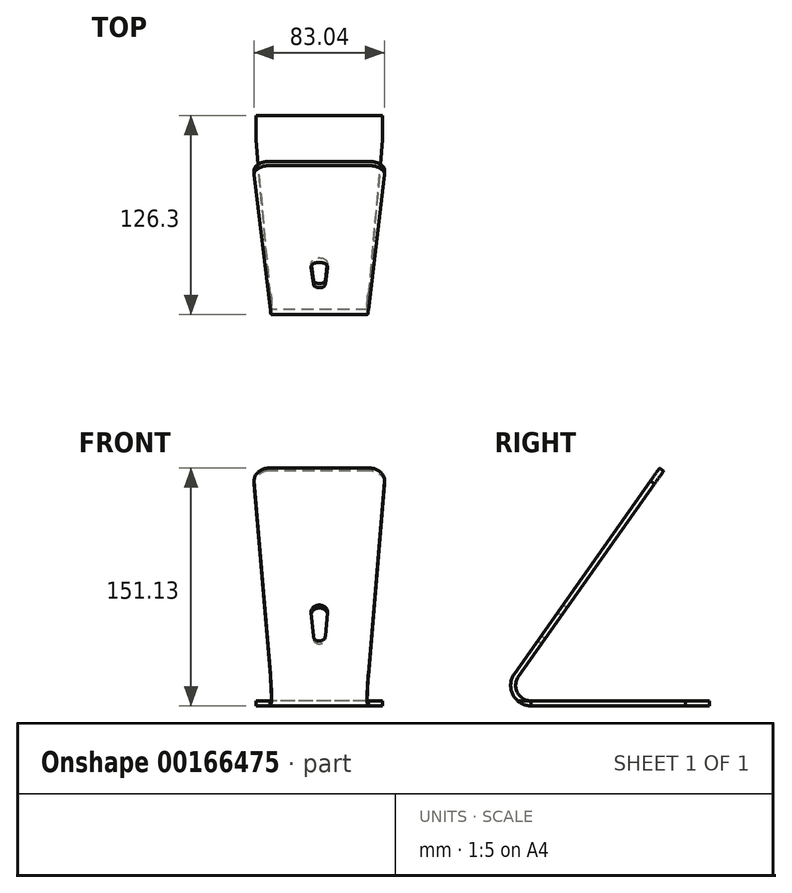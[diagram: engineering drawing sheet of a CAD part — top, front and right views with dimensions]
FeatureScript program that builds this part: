
annotation { "Feature Type Name" : "Feature", "Feature Type Description" : "" }
export const myFeature = defineFeature(function(context is Context, id is Id, definition is map)
    precondition{}
    {
        {
            var Q0;
            Q0=qCreatedBy(makeId("Right.planeOp"),FACE);
            var sketch = newSketch(context, id + "F0", { "sketchPlane" : qUnion([Q0])});
            skLineSegment(sketch, "E0.bottom", {"start": v(17.3, 0) * mm, "end": v(130.65, 0) * mm});
            skLineSegment(sketch, "E0.top", {"start": v(17.3, 3.18) * mm, "end": v(130.65, 3.18) * mm});
            skLineSegment(sketch, "E0.right", {"start": v(130.65, 0) * mm, "end": v(130.65, 3.18) * mm});
            skLineSegment(sketch, "E1", {"start": v(9.32, 18.6) * mm, "end": v(101.55, 149.3) * mm});
            skLineSegment(sketch, "E2", {"start": v(101.55, 149.3) * mm, "end": v(98.96, 151.13) * mm});
            skLineSegment(sketch, "E3", {"start": v(98.96, 151.13) * mm, "end": v(6.72, 20.42) * mm});
            skArc(sketch, "E4.filletArc", {"start": v(9.32, 18.6) * mm, "mid": v(8.63, 8.45) * mm, "end": v(17.3, 3.18) * mm});
            skPoint(sketch, "E5.newPointB", {"position": v(0, 0) * mm});
            skArc(sketch, "E5.filletArc", {"start": v(6.72, 20.42) * mm, "mid": v(5.8, 7) * mm, "end": v(17.3, 0) * mm});
            skLineSegment(sketch, "E6", {"start": v(98.96, 151.13) * mm, "end": v(98.96, 0) * mm});
            skLineSegment(sketch, "E7", {"start": v(130.65, 0) * mm, "end": v(38.3, 65.17) * mm});
            skLineSegment(sketch, "E8", {"start": v(98.96, 0) * mm, "end": v(17.3, 0) * mm});
            skSolve(sketch);
        }
        {
            var Q0;
            {var subQ0=sQuery(id+"F0.wireOp",EDGE,"E6");var subQ1=sQuery(id+"F0.wireOp",EDGE,"E1");var subQ2=makeQuery(id+"F0.imprint","INTERSECT",VERTEX,{"derivedFrom":[subQ1,subQ0]});Q0=makeQuery(id+"F0.imprint","IMPRINT",FACE,{"disambiguationData":[TD([[makeQuery(id+"F0.imprint","IMPRINT",EDGE,{"disambiguationData":[TD([[subQ2,1.0]])],"derivedFrom":subQ1}),1.0]])]});}
            var Q1;
            {var subQ4=sQuery(id+"F0.wireOp",EDGE,"E4.filletArc");Q1=makeQuery(id+"F0.imprint","IMPRINT",FACE,{"disambiguationData":[TD([[makeQuery(id+"F0.imprint","IMPRINT",EDGE,{"derivedFrom":subQ4}),-1.0]])]});}
            var Q2;
            {var subQ0=sQuery(id+"F0.wireOp",EDGE,"E7");var subQ5=sQuery(id+"F0.wireOp",EDGE,"E0.top");var subQ6=makeQuery(id+"F0.imprint","INTERSECT",VERTEX,{"derivedFrom":[subQ5,subQ0]});Q2=makeQuery(id+"F0.imprint","IMPRINT",FACE,{"disambiguationData":[TD([[makeQuery(id+"F0.imprint","IMPRINT",EDGE,{"disambiguationData":[TD([[subQ6,1.0]])],"derivedFrom":subQ5}),-1.0]])]});}
            var Q3;
            {var subQ0=sQuery(id+"F0.wireOp",EDGE,"E0.right");Q3=makeQuery(id+"F0.imprint","IMPRINT",FACE,{"disambiguationData":[TD([[makeQuery(id+"F0.imprint","IMPRINT",EDGE,{"derivedFrom":subQ0}),1.0]])]});}
            var Q4;
            {var subQ0=sQuery(id+"F0.wireOp",EDGE,"E2");Q4=makeQuery(id+"F0.imprint","IMPRINT",FACE,{"disambiguationData":[TD([[makeQuery(id+"F0.imprint","IMPRINT",EDGE,{"derivedFrom":subQ0}),1.0]])]});}
            extrude(context, id + "F1", {"entities" : qUnion([Q0, Q1, Q2, Q3, Q4]), "endBound" : BoundingType.SYMMETRIC, "depth" : 83.03 * mm});
        }
        {
            var Q0;
            Q0=makeQuery(id+"F1.opExtrude","CAP_EDGE",EDGE,{"disambiguationData":[OSD([sQuery(id+"F0.wireOp",EDGE,"E2")])],"isStart":true});
            var Q1;
            Q1=makeQuery(id+"F1.opExtrude","CAP_EDGE",EDGE,{"disambiguationData":[OSD([sQuery(id+"F0.wireOp",EDGE,"E2")])],"isStart":false});
            fillet(context, id + "F2", {"entities" : qUnion([Q0, Q1]), "radius" : 10.16 * mm, "tangentPropagation" : true, "allowEdgeOverflow" : false});
        }
        {
            var Q0;
            Q0=makeQuery(id+"F1.opExtrude","SWEPT_FACE",FACE,{"disambiguationData":[OSD([sQuery(id+"F0.wireOp",EDGE,"E3")])]});
            var sketch = newSketch(context, id + "F3", { "sketchPlane" : qUnion([Q0])});
            skLineSegment(sketch, "E9", {"start": v(31.12, 20.56) * mm, "end": v(41.52, 170.38) * mm});
            skLineSegment(sketch, "E10", {"start": v(-31.12, 20.56) * mm, "end": v(-41.52, 170.38) * mm});
            skLineSegment(sketch, "E11", {"start": v(-31.12, 20.56) * mm, "end": v(31.12, 20.56) * mm});
            skLineSegment(sketch, "E12", {"start": v(0, -1.58) * mm, "end": v(0, 20.56) * mm});
            skLineSegment(sketch, "E13", {"start": v(31.12, 20.56) * mm, "end": v(41.52, 20.56) * mm});
            skLineSegment(sketch, "E14", {"start": v(-31.12, 20.56) * mm, "end": v(-41.52, 20.56) * mm});
            skLineSegment(sketch, "E15", {"start": v(41.52, 20.56) * mm, "end": v(41.52, 170.38) * mm});
            skLineSegment(sketch, "E16", {"start": v(-41.52, 170.38) * mm, "end": v(-41.52, 20.56) * mm});
            skLineSegment(sketch, "E17", {"start": v(31.12, 20.56) * mm, "end": v(29.58, -1.58) * mm});
            skLineSegment(sketch, "E18", {"start": v(29.58, -1.58) * mm, "end": v(41.52, -1.58) * mm});
            skLineSegment(sketch, "E19", {"start": v(41.52, -1.58) * mm, "end": v(41.52, 20.56) * mm});
            skLineSegment(sketch, "E20.MirrorCS", {"start": v(-31.12, 20.56) * mm, "end": v(-29.58, -1.58) * mm});
            skLineSegment(sketch, "E21.MirrorCS", {"start": v(-29.58, -1.58) * mm, "end": v(-41.52, -1.58) * mm});
            skLineSegment(sketch, "E22.MirrorCS", {"start": v(-41.52, -1.58) * mm, "end": v(-41.52, 20.56) * mm});
            skSolve(sketch);
        }
        {
            var Q0;
            Q0 = qSketchRegion(id + "F3", true);
            var Q1;
            Q1=makeQuery(id+"F1.opExtrude","SWEPT_FACE",FACE,{"disambiguationData":[OSD([sQuery(id+"F0.wireOp",EDGE,"E0.top")])]});
            extrude(context, id + "F4", {"entities" : qUnion([Q0]), "operationType" : NewBodyOperationType.REMOVE, "endBound" : BoundingType.UP_TO_SURFACE, "oppositeDirection" : true, "endBoundEntityFace" : qUnion([Q1]), "depth" : 25.4 * mm});
        }
        {
            var Q0;
            Q0=makeQuery(id+"F1.opExtrude","SWEPT_FACE",FACE,{"disambiguationData":[OSD([sQuery(id+"F0.wireOp",EDGE,"E3")])]});
            var sketch = newSketch(context, id + "F5", { "sketchPlane" : qUnion([Q0])});
            skCircle(sketch, "E23", {"center": v(0, 68.72) * mm, "radius": 5.18 * mm});
            skCircle(sketch, "E24", {"center": v(0, 49.77) * mm, "radius": 3.81 * mm});
            skLineSegment(sketch, "E25", {"start": v(3.8, 49.77) * mm, "end": v(5.18, 68.72) * mm});
            skLineSegment(sketch, "E26", {"start": v(-5.18, 68.72) * mm, "end": v(-3.81, 49.77) * mm});
            skLineSegment(sketch, "E27", {"start": v(0, 20.56) * mm, "end": v(0, 45.96) * mm});
            skLineSegment(sketch, "E28", {"start": v(0, 45.96) * mm, "end": v(0, 73.9) * mm});
            skSolve(sketch);
        }
        {
            var Q0;
            Q0 = qSketchRegion(id + "F5", true);
            var Q1;
            Q1=makeQuery(id+"F1.opExtrude","SWEPT_FACE",FACE,{"disambiguationData":[OSD([sQuery(id+"F0.wireOp",EDGE,"E1")])]});
            extrude(context, id + "F6", {"entities" : qUnion([Q0]), "operationType" : NewBodyOperationType.REMOVE, "endBound" : BoundingType.UP_TO_SURFACE, "oppositeDirection" : true, "endBoundEntityFace" : qUnion([Q1]), "depth" : 25.4 * mm});
        }
        {
            var Q0;
            Q0=makeQuery(id+"F1.opExtrude","SWEPT_FACE",FACE,{"disambiguationData":[OSD([sQuery(id+"F0.wireOp",EDGE,"E0.top")])]});
            var sketch = newSketch(context, id + "F7", { "sketchPlane" : qUnion([Q0])});
            skLineSegment(sketch, "E29", {"start": v(-41.52, 130.65) * mm, "end": v(-40.25, 130.65) * mm});
            skLineSegment(sketch, "E30.left", {"start": v(-40.25, 130.65) * mm, "end": v(-40.25, 14.6) * mm});
            skLineSegment(sketch, "E30.right", {"start": v(40.25, 130.65) * mm, "end": v(40.25, 17.3) * mm});
            skLineSegment(sketch, "E31", {"start": v(40.25, 130.65) * mm, "end": v(41.52, 130.65) * mm});
            skLineSegment(sketch, "E32", {"start": v(-40.25, 14.6) * mm, "end": v(-41.52, 14.6) * mm});
            skLineSegment(sketch, "E33", {"start": v(-41.52, 14.6) * mm, "end": v(-41.52, 130.65) * mm});
            skLineSegment(sketch, "E34", {"start": v(40.25, 17.3) * mm, "end": v(41.52, 17.3) * mm});
            skLineSegment(sketch, "E35", {"start": v(41.52, 17.3) * mm, "end": v(41.52, 130.65) * mm});
            skSolve(sketch);
        }
        {
            var Q0;
            Q0 = qSketchRegion(id + "F7", true);
            var Q1;
            Q1=makeQuery(id+"F1.opExtrude","SWEPT_FACE",FACE,{"disambiguationData":[OSD([sQuery(id+"F0.wireOp",EDGE,"E0.bottom"),sQuery(id+"F0.wireOp",EDGE,"E8")])]});
            extrude(context, id + "F8", {"entities" : qUnion([Q0]), "operationType" : NewBodyOperationType.REMOVE, "endBound" : BoundingType.UP_TO_SURFACE, "oppositeDirection" : true, "endBoundEntityFace" : qUnion([Q1]), "depth" : 25.4 * mm});
        }
        {
            var Q0;
            Q0=makeQuery(id+"F8.boolean.opBoolean","COPY",EDGE,{"derivedFrom":makeQuery(id+"F8.opExtrude","SWEPT_EDGE",EDGE,{"disambiguationData":[OSD([sQuery(id+"F0.wireOp",EDGE,"E0.top"),sQuery(id+"F7.wireOp",EDGE,"E30.right"),sQuery(id+"F7.wireOp",EDGE,"E31")])]})});
            var Q1;
            Q1=makeQuery(id+"F8.boolean.opBoolean","COPY",EDGE,{"derivedFrom":makeQuery(id+"F8.opExtrude","SWEPT_EDGE",EDGE,{"disambiguationData":[OSD([sQuery(id+"F0.wireOp",EDGE,"E0.top"),sQuery(id+"F7.wireOp",EDGE,"E29"),sQuery(id+"F7.wireOp",EDGE,"E30.left")])]})});
            fillet(context, id + "F9", {"entities" : qUnion([Q0, Q1]), "radius" : 15.24 * mm, "tangentPropagation" : true, "allowEdgeOverflow" : false});
        }
        {
            var Q0;
            Q0=makeQuery(id+"F1.opExtrude","SWEPT_FACE",FACE,{"disambiguationData":[OSD([sQuery(id+"F0.wireOp",EDGE,"E0.top")])]});
            var sketch = newSketch(context, id + "F10", { "sketchPlane" : qUnion([Q0])});
            skLineSegment(sketch, "E36", {"start": v(0, 0) * mm, "end": v(0, 17.3) * mm});
            skLineSegment(sketch, "E37", {"start": v(-31.37, 17.3) * mm, "end": v(31.37, 17.3) * mm});
            skLineSegment(sketch, "E38", {"start": v(31.37, 17.3) * mm, "end": v(40.25, 115.41) * mm});
            skLineSegment(sketch, "E39", {"start": v(-31.37, 17.3) * mm, "end": v(-40.25, 115.41) * mm});
            skLineSegment(sketch, "E40", {"start": v(-40.25, 115.41) * mm, "end": v(-40.25, 14.6) * mm});
            skLineSegment(sketch, "E41", {"start": v(31.37, 17.3) * mm, "end": v(30.22, 8.81) * mm});
            skLineSegment(sketch, "E42", {"start": v(30.22, 8.81) * mm, "end": v(41.52, 8.81) * mm});
            skLineSegment(sketch, "E43", {"start": v(41.52, 8.81) * mm, "end": v(41.52, 115.41) * mm});
            skLineSegment(sketch, "E44", {"start": v(41.52, 115.41) * mm, "end": v(40.25, 115.41) * mm});
            skLineSegment(sketch, "E45.MirrorCS", {"start": v(-30.22, 8.81) * mm, "end": v(-41.52, 8.81) * mm});
            skLineSegment(sketch, "E46.MirrorCS", {"start": v(-31.37, 17.3) * mm, "end": v(-30.22, 8.81) * mm});
            skLineSegment(sketch, "E47.MirrorCS", {"start": v(-41.52, 8.81) * mm, "end": v(-41.52, 115.41) * mm});
            skLineSegment(sketch, "E48.MirrorCS", {"start": v(-41.52, 115.41) * mm, "end": v(-40.25, 115.41) * mm});
            skSolve(sketch);
        }
        {
            var Q0;
            Q0 = qSketchRegion(id + "F10", true);
            var Q1;
            Q1=makeQuery(id+"F1.opExtrude","SWEPT_FACE",FACE,{"disambiguationData":[OSD([sQuery(id+"F0.wireOp",EDGE,"E0.bottom"),sQuery(id+"F0.wireOp",EDGE,"E8")])]});
            extrude(context, id + "F11", {"entities" : qUnion([Q0]), "operationType" : NewBodyOperationType.REMOVE, "endBound" : BoundingType.UP_TO_SURFACE, "oppositeDirection" : true, "endBoundEntityFace" : qUnion([Q1]), "depth" : 25.4 * mm});
        }
    });
